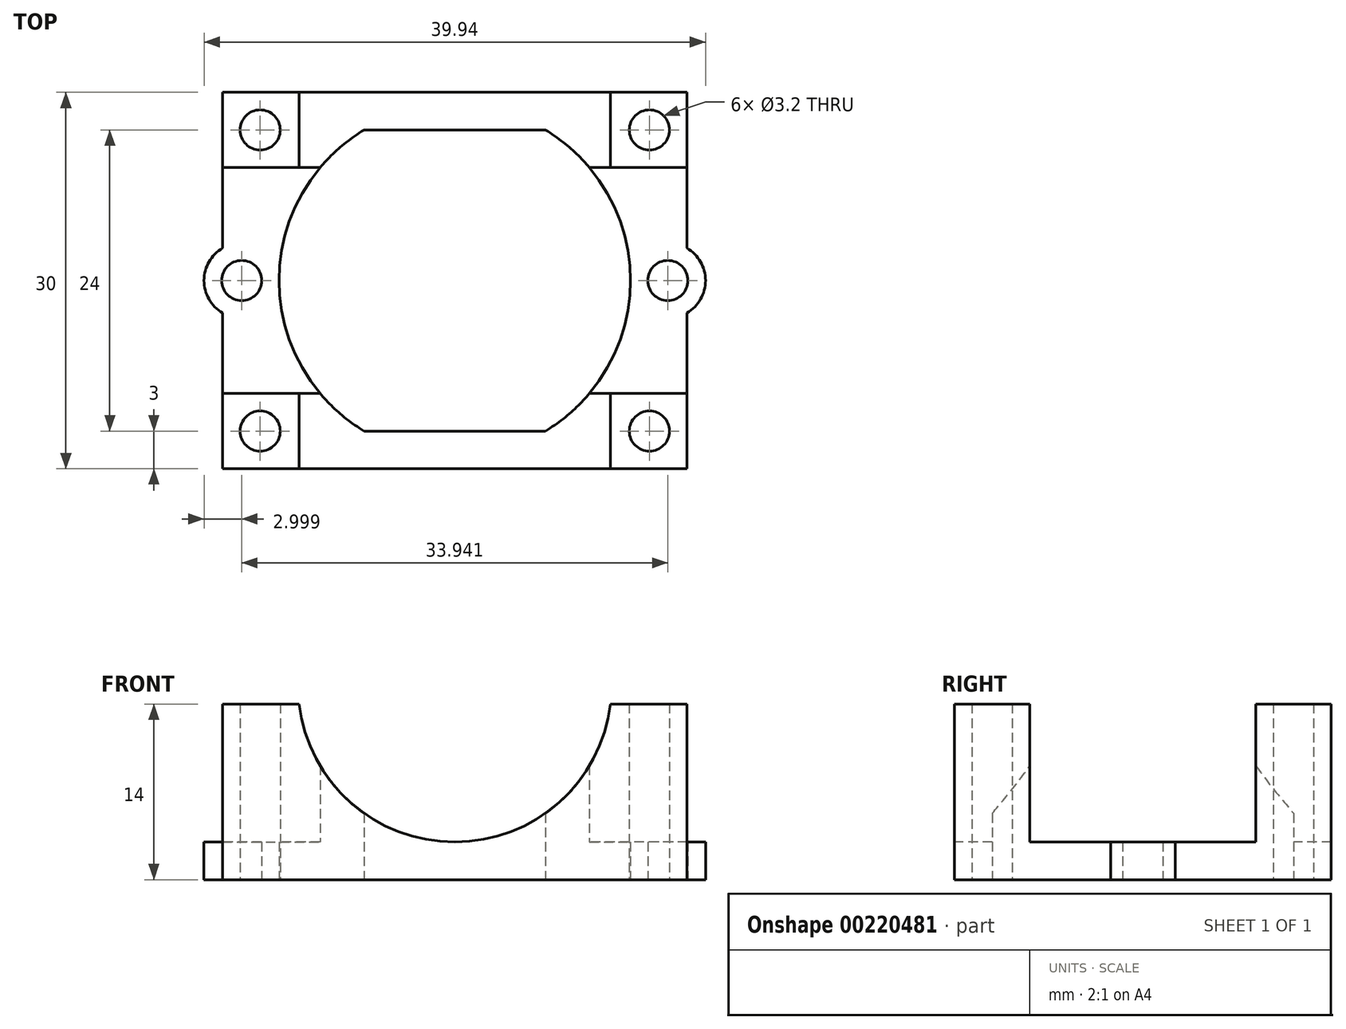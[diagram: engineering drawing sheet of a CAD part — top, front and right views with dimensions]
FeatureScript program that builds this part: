
annotation { "Feature Type Name" : "Feature", "Feature Type Description" : "" }
export const myFeature = defineFeature(function(context is Context, id is Id, definition is map)
    precondition{}
    {
        {
            var Q0;
            Q0=qCreatedBy(makeId("Top.planeOp"),FACE);
            var sketch = newSketch(context, id + "F0", { "sketchPlane" : qUnion([Q0])});
            skLineSegment(sketch, "E0.bottom", {"start": v(-18.5, 15) * mm, "end": v(18.5, 15) * mm});
            skLineSegment(sketch, "E0.top", {"start": v(-18.5, -15) * mm, "end": v(18.5, -15) * mm});
            skLineSegment(sketch, "E0.left", {"start": v(-18.5, 15) * mm, "end": v(-18.5, -15) * mm, "construction": true});
            skLineSegment(sketch, "E0.right", {"start": v(18.5, 15) * mm, "end": v(18.5, -15) * mm, "construction": true});
            skLineSegment(sketch, "E1", {"start": v(-18.5, 15) * mm, "end": v(18.5, -15) * mm, "construction": true});
            skLineSegment(sketch, "E2.bottom", {"start": v(-14, 12) * mm, "end": v(14, 12) * mm, "construction": true});
            skLineSegment(sketch, "E2.top", {"start": v(-14, -12) * mm, "end": v(14, -12) * mm, "construction": true});
            skLineSegment(sketch, "E2.left", {"start": v(-14, 12) * mm, "end": v(-14, -12) * mm, "construction": true});
            skLineSegment(sketch, "E2.right", {"start": v(14, 12) * mm, "end": v(14, -12) * mm, "construction": true});
            skArc(sketch, "E3", {"start": v(7.21, 12) * mm, "mid": v(14, 0) * mm, "end": v(7.21, -12) * mm});
            skArc(sketch, "E4", {"start": v(-7.21, 12) * mm, "mid": v(-14, 0) * mm, "end": v(-7.21, -12) * mm});
            skLineSegment(sketch, "E5", {"start": v(-7.21, 12) * mm, "end": v(7.21, 12) * mm});
            skLineSegment(sketch, "E6", {"start": v(7.21, -12) * mm, "end": v(-7.21, -12) * mm});
            skLineSegment(sketch, "E7", {"start": v(-16.97, 0) * mm, "end": v(0, 16.97) * mm, "construction": true});
            skLineSegment(sketch, "E8", {"start": v(0, 16.97) * mm, "end": v(16.97, 0) * mm, "construction": true});
            skLineSegment(sketch, "E9", {"start": v(16.97, 0) * mm, "end": v(0, -16.97) * mm, "construction": true});
            skLineSegment(sketch, "E10", {"start": v(0, -16.97) * mm, "end": v(-16.97, 0) * mm, "construction": true});
            skArc(sketch, "E11", {"start": v(-18.5, 2.58) * mm, "mid": v(-19.97, 0) * mm, "end": v(-18.5, -2.58) * mm});
            skArc(sketch, "E12", {"start": v(18.5, 2.58) * mm, "mid": v(19.97, 0) * mm, "end": v(18.5, -2.58) * mm});
            skLineSegment(sketch, "E13", {"start": v(-18.5, 2.58) * mm, "end": v(-18.5, 15) * mm});
            skLineSegment(sketch, "E14", {"start": v(-18.5, -2.58) * mm, "end": v(-18.5, -15) * mm});
            skLineSegment(sketch, "E15", {"start": v(18.5, 15) * mm, "end": v(18.5, 2.58) * mm});
            skLineSegment(sketch, "E16", {"start": v(18.5, -2.58) * mm, "end": v(18.5, -15) * mm});
            skSolve(sketch);
        }
        {
            var Q0;
            Q0 = qSketchRegion(id + "F0", true);
            extrude(context, id + "F1", {"entities" : qUnion([Q0]), "depth" : 3 * mm});
        }
        {
            var Q0;
            Q0=makeQuery(id+"F1.opExtrude","CAP_FACE",FACE,{"disambiguationData":[OSD([sQuery(id+"F0.wireOp",EDGE,"E0.bottom"),sQuery(id+"F0.wireOp",EDGE,"E0.top"),sQuery(id+"F0.wireOp",EDGE,"E0.left"),sQuery(id+"F0.wireOp",EDGE,"E0.right"),sQuery(id+"F0.wireOp",EDGE,"E3"),sQuery(id+"F0.wireOp",EDGE,"E4"),sQuery(id+"F0.wireOp",EDGE,"E5"),sQuery(id+"F0.wireOp",EDGE,"E6")])],"isStart":false});
            var sketch = newSketch(context, id + "F2", { "sketchPlane" : qUnion([Q0])});
            skLineSegment(sketch, "E17", {"start": v(-18.5, 15) * mm, "end": v(-18.5, 9) * mm});
            skLineSegment(sketch, "E18", {"start": v(-18.5, 9) * mm, "end": v(-10.72, 9) * mm});
            skLineSegment(sketch, "E19", {"start": v(-7.21, 12) * mm, "end": v(7.21, 12) * mm});
            skLineSegment(sketch, "E20", {"start": v(7.21, -12) * mm, "end": v(-7.21, -12) * mm});
            skLineSegment(sketch, "E21", {"start": v(-18.5, -9) * mm, "end": v(-18.5, -15) * mm});
            skArc(sketch, "E22", {"start": v(7.21, 12) * mm, "mid": v(9.1, 10.65) * mm, "end": v(10.72, 9) * mm});
            skArc(sketch, "E23", {"start": v(7.21, -12) * mm, "mid": v(9.1, -10.65) * mm, "end": v(10.72, -9) * mm});
            skArc(sketch, "E24", {"start": v(-7.21, -12) * mm, "mid": v(-9.1, -10.65) * mm, "end": v(-10.72, -9) * mm});
            skArc(sketch, "E25", {"start": v(-7.21, 12) * mm, "mid": v(-9.1, 10.65) * mm, "end": v(-10.72, 9) * mm});
            skLineSegment(sketch, "E26", {"start": v(-18.5, 15) * mm, "end": v(18.5, 15) * mm});
            skLineSegment(sketch, "E27", {"start": v(18.5, 15) * mm, "end": v(18.5, 9) * mm});
            skLineSegment(sketch, "E28", {"start": v(-18.5, -15) * mm, "end": v(18.5, -15) * mm});
            skLineSegment(sketch, "E29", {"start": v(18.5, 9) * mm, "end": v(10.72, 9) * mm});
            skLineSegment(sketch, "E30", {"start": v(-18.5, -9) * mm, "end": v(-10.72, -9) * mm});
            skLineSegment(sketch, "E31", {"start": v(18.5, -15) * mm, "end": v(18.5, -9) * mm});
            skLineSegment(sketch, "E32", {"start": v(18.5, -9) * mm, "end": v(10.72, -9) * mm});
            skSolve(sketch);
        }
        {
            var Q0;
            Q0 = qSketchRegion(id + "F2", true);
            extrude(context, id + "F3", {"entities" : qUnion([Q0]), "operationType" : NewBodyOperationType.ADD, "depth" : 11 * mm});
        }
        {
            var Q0;
            Q0=makeQuery(id+"F3.boolean.opBoolean","MERGE",FACE,{"derivedFrom":[makeQuery(id+"F1.opExtrude","SWEPT_FACE",FACE,{"disambiguationData":[OSD([sQuery(id+"F0.wireOp",EDGE,"E0.top")])]}),makeQuery(id+"F3.opExtrude","SWEPT_FACE",FACE,{"disambiguationData":[OSD([sQuery(id+"F2.wireOp",EDGE,"xNLFnr0d-gIlK-BfzF-xgm5-FjT9KyOfp67Z")])]})]});
            var sketch = newSketch(context, id + "F4", { "sketchPlane" : qUnion([Q0])});
            skArc(sketch, "E33", {"start": v(-12.4, 14) * mm, "mid": v(0, 3) * mm, "end": v(12.4, 14) * mm});
            skLineSegment(sketch, "E34", {"start": v(-12.4, 14) * mm, "end": v(12.4, 14) * mm});
            skLineSegment(sketch, "E35", {"start": v(0, 0) * mm, "end": v(0, 3) * mm, "construction": true});
            skSolve(sketch);
        }
        {
            var Q0;
            Q0 = qSketchRegion(id + "F4", true);
            extrude(context, id + "F5", {"entities" : qUnion([Q0]), "operationType" : NewBodyOperationType.REMOVE, "endBound" : BoundingType.THROUGH_ALL, "oppositeDirection" : true, "depth" : 25 * mm});
        }
        {
            var Q0;
            Q0=makeQuery(id+"F1.opExtrude","CAP_FACE",FACE,{"disambiguationData":[OSD([sQuery(id+"F0.wireOp",EDGE,"E0.bottom"),sQuery(id+"F0.wireOp",EDGE,"E0.top"),sQuery(id+"F0.wireOp",EDGE,"E3"),sQuery(id+"F0.wireOp",EDGE,"E4"),sQuery(id+"F0.wireOp",EDGE,"E5"),sQuery(id+"F0.wireOp",EDGE,"E6"),sQuery(id+"F0.wireOp",EDGE,"E11"),sQuery(id+"F0.wireOp",EDGE,"E12"),sQuery(id+"F0.wireOp",EDGE,"E13"),sQuery(id+"F0.wireOp",EDGE,"E14"),sQuery(id+"F0.wireOp",EDGE,"E15"),sQuery(id+"F0.wireOp",EDGE,"E16")])],"isStart":true});
            var sketch = newSketch(context, id + "F6", { "sketchPlane" : qUnion([Q0])});
            skLineSegment(sketch, "E36.bottom", {"start": v(-15.5, 12) * mm, "end": v(15.5, 12) * mm, "construction": true});
            skLineSegment(sketch, "E36.top", {"start": v(-15.5, -12) * mm, "end": v(15.5, -12) * mm, "construction": true});
            skLineSegment(sketch, "E36.left", {"start": v(-15.5, 12) * mm, "end": v(-15.5, -12) * mm, "construction": true});
            skLineSegment(sketch, "E36.right", {"start": v(15.5, 12) * mm, "end": v(15.5, -12) * mm, "construction": true});
            skCircle(sketch, "E37", {"center": v(-15.5, 12) * mm, "radius": 1.6 * mm});
            skCircle(sketch, "E38", {"center": v(15.5, 12) * mm, "radius": 1.6 * mm});
            skCircle(sketch, "E39", {"center": v(15.5, -12) * mm, "radius": 1.6 * mm});
            skCircle(sketch, "E40", {"center": v(-15.5, -12) * mm, "radius": 1.6 * mm});
            skCircle(sketch, "E41", {"center": v(-16.97, 0) * mm, "radius": 1.6 * mm});
            skCircle(sketch, "E42", {"center": v(16.97, 0) * mm, "radius": 1.6 * mm});
            skSolve(sketch);
        }
        {
            var Q0;
            Q0 = qSketchRegion(id + "F6", true);
            extrude(context, id + "F7", {"entities" : qUnion([Q0]), "operationType" : NewBodyOperationType.REMOVE, "endBound" : BoundingType.THROUGH_ALL, "oppositeDirection" : true, "depth" : 25 * mm});
        }
    });
